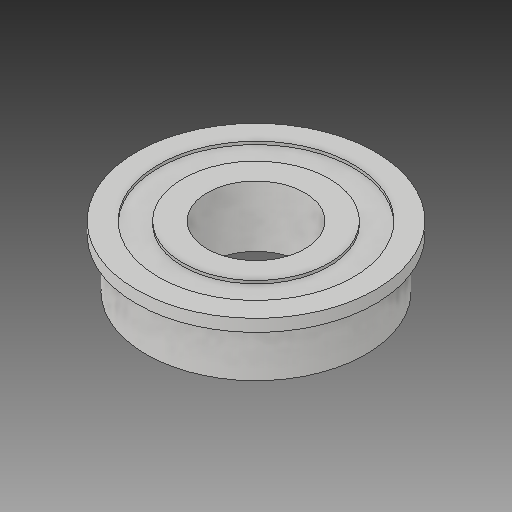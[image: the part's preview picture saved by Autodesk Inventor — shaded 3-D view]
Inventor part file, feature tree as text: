
AUTODESK INVENTOR PART (.ipt)
format: ipt  version: 2017 (Build 210142000, 142)  size: 118,272 bytes
history: native  units: in
note: dims shown in document units (in); Inventor stores cm internally (conversion verified against a paired STEP export)
features: revolve x1
ambient origin geometry x8: Origin, YZ Plane, XZ Plane, XY Plane, X Axis, Y Axis, Z Axis, Center Point
bodies: Solid1 (feature_tree)
feature tree (1):
  revolve  "Revolve1"  [1 undecoded]
note: 1 required parameter value undecoded (feature->parameter linkage not recoverable at this tier; creation-order binding heuristic only, values carry confidence <= 0.55)
